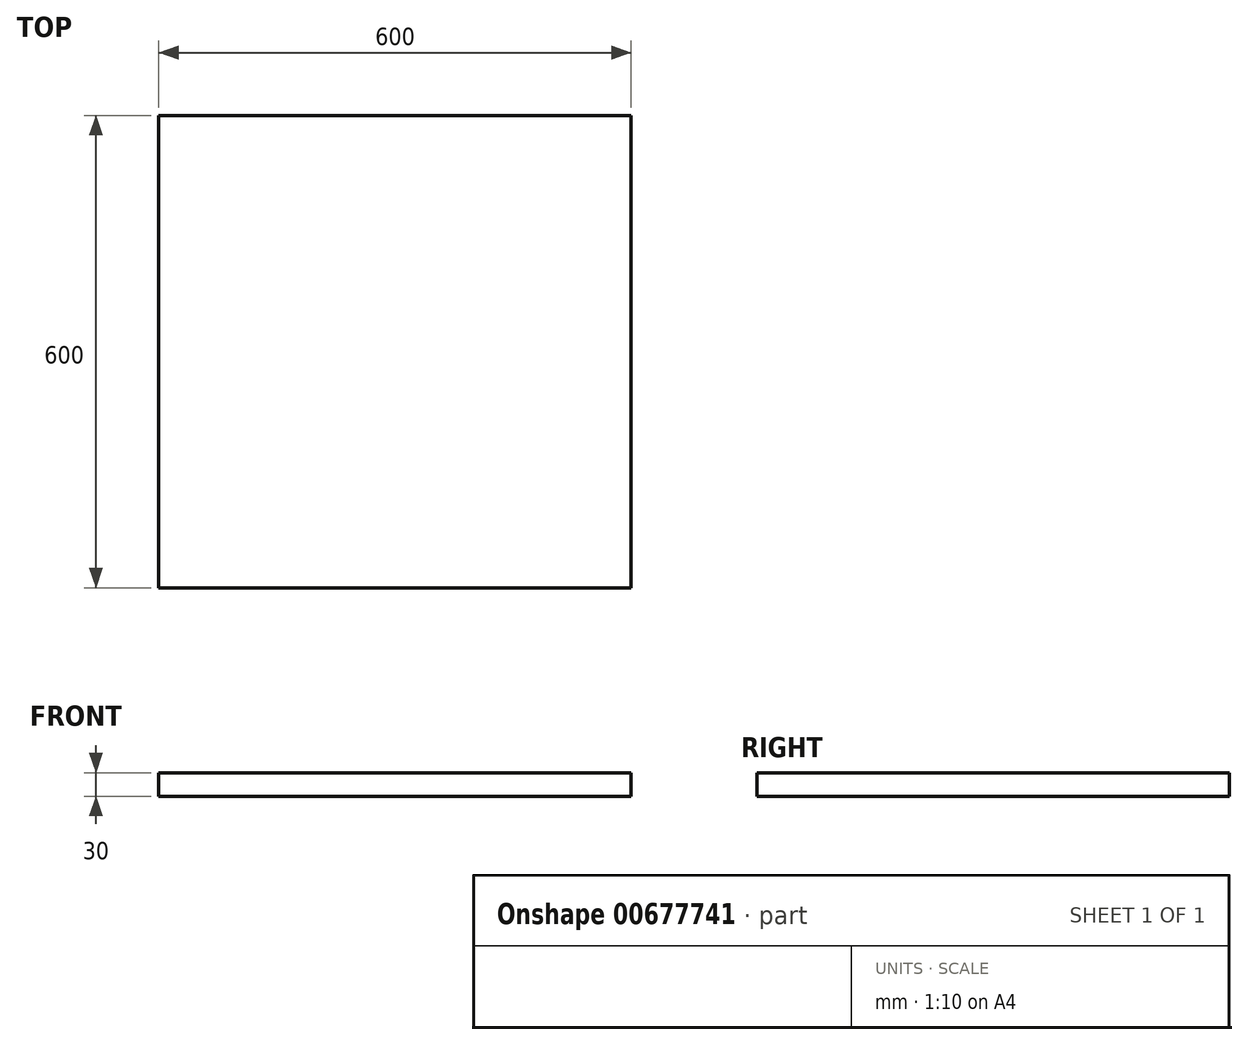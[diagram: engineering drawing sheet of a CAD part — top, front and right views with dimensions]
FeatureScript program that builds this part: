
annotation { "Feature Type Name" : "Feature", "Feature Type Description" : "" }
export const myFeature = defineFeature(function(context is Context, id is Id, definition is map)
    precondition{}
    {
        {
            var Q0;
            Q0=qCreatedBy(makeId("Top.planeOp"),FACE);
            var sketch = newSketch(context, id + "F0", { "sketchPlane" : qUnion([Q0])});
            skLineSegment(sketch, "E0.bottom", {"start": v(0, 0) * mm, "end": v(600, 0) * mm});
            skLineSegment(sketch, "E0.top", {"start": v(0, 600) * mm, "end": v(600, 600) * mm});
            skLineSegment(sketch, "E0.left", {"start": v(0, 0) * mm, "end": v(0, 600) * mm});
            skLineSegment(sketch, "E0.right", {"start": v(600, 0) * mm, "end": v(600, 600) * mm});
            skPoint(sketch, "E1", {"position": v(0, 0) * mm});
            skSolve(sketch);
        }
        {
            var Q0;
            Q0=makeQuery(id+"F0.imprint","IMPRINT",FACE,{"disambiguationData":[TD([[makeQuery(id+"F0.imprint","IMPRINT",EDGE,{"derivedFrom":sQuery(id+"F0.wireOp",EDGE,"E0.bottom")}),1.0]])]});
            extrude(context, id + "F1", {"entities" : qUnion([Q0]), "depth" : 30 * mm, "offsetDistance" : 25 * mm});
        }
    });
